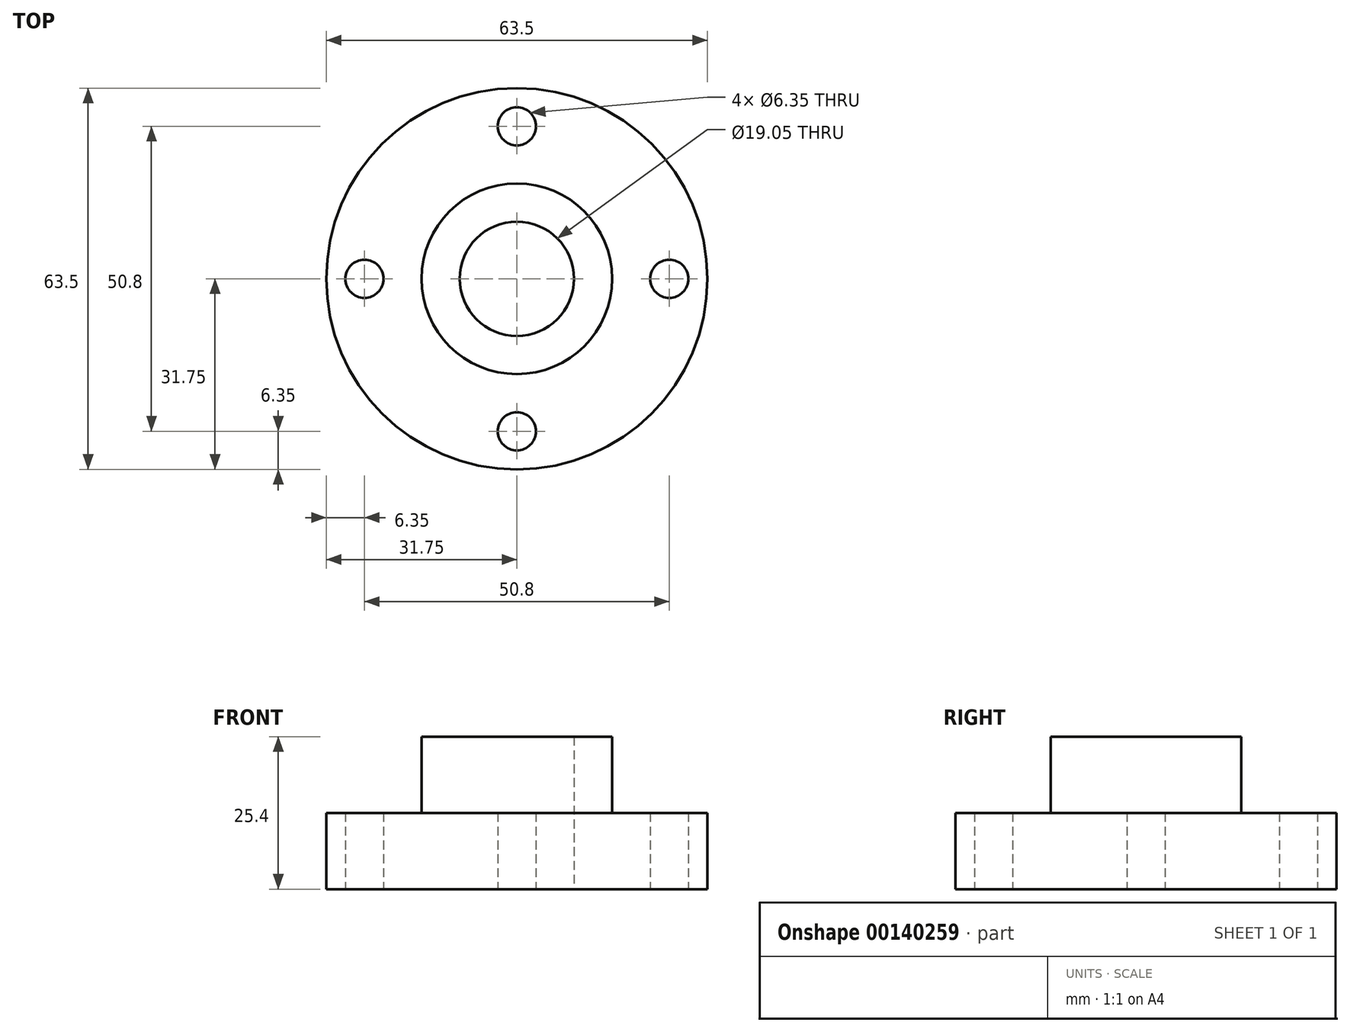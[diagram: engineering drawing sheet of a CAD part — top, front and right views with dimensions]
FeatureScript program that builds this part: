
annotation { "Feature Type Name" : "Feature", "Feature Type Description" : "" }
export const myFeature = defineFeature(function(context is Context, id is Id, definition is map)
    precondition{}
    {
        {
            var Q0;
            Q0=qCreatedBy(makeId("Top.planeOp"),FACE);
            var sketch = newSketch(context, id + "F0", { "sketchPlane" : qUnion([Q0])});
            skCircle(sketch, "E0", {"center": v(0, 0) * mm, "radius": 31.75 * mm});
            skCircle(sketch, "E1", {"center": v(0, 0) * mm, "radius": 15.88 * mm});
            skCircle(sketch, "E2", {"center": v(-25.4, 0) * mm, "radius": 3.18 * mm});
            skCircle(sketch, "E3", {"center": v(0, 25.4) * mm, "radius": 3.18 * mm});
            skCircle(sketch, "E4", {"center": v(25.4, 0) * mm, "radius": 3.18 * mm});
            skCircle(sketch, "E5", {"center": v(0, -25.4) * mm, "radius": 3.18 * mm});
            skCircle(sketch, "E6", {"center": v(0, 0) * mm, "radius": 9.53 * mm});
            skSolve(sketch);
        }
        {
            var Q0;
            Q0=makeQuery(id+"F0.imprint","IMPRINT",FACE,{"disambiguationData":[TD([[makeQuery(id+"F0.imprint","IMPRINT",EDGE,{"derivedFrom":sQuery(id+"F0.wireOp",EDGE,"E0")}),1.0]])]});
            extrude(context, id + "F1", {"entities" : qUnion([Q0]), "depth" : 12.7 * mm});
        }
        {
            var Q0;
            Q0=makeQuery(id+"F0.imprint","IMPRINT",FACE,{"disambiguationData":[TD([[makeQuery(id+"F0.imprint","IMPRINT",EDGE,{"derivedFrom":sQuery(id+"F0.wireOp",EDGE,"E1")}),1.0]])]});
            extrude(context, id + "F2", {"entities" : qUnion([Q0]), "operationType" : NewBodyOperationType.ADD, "depth" : 25.4 * mm});
        }
    });
